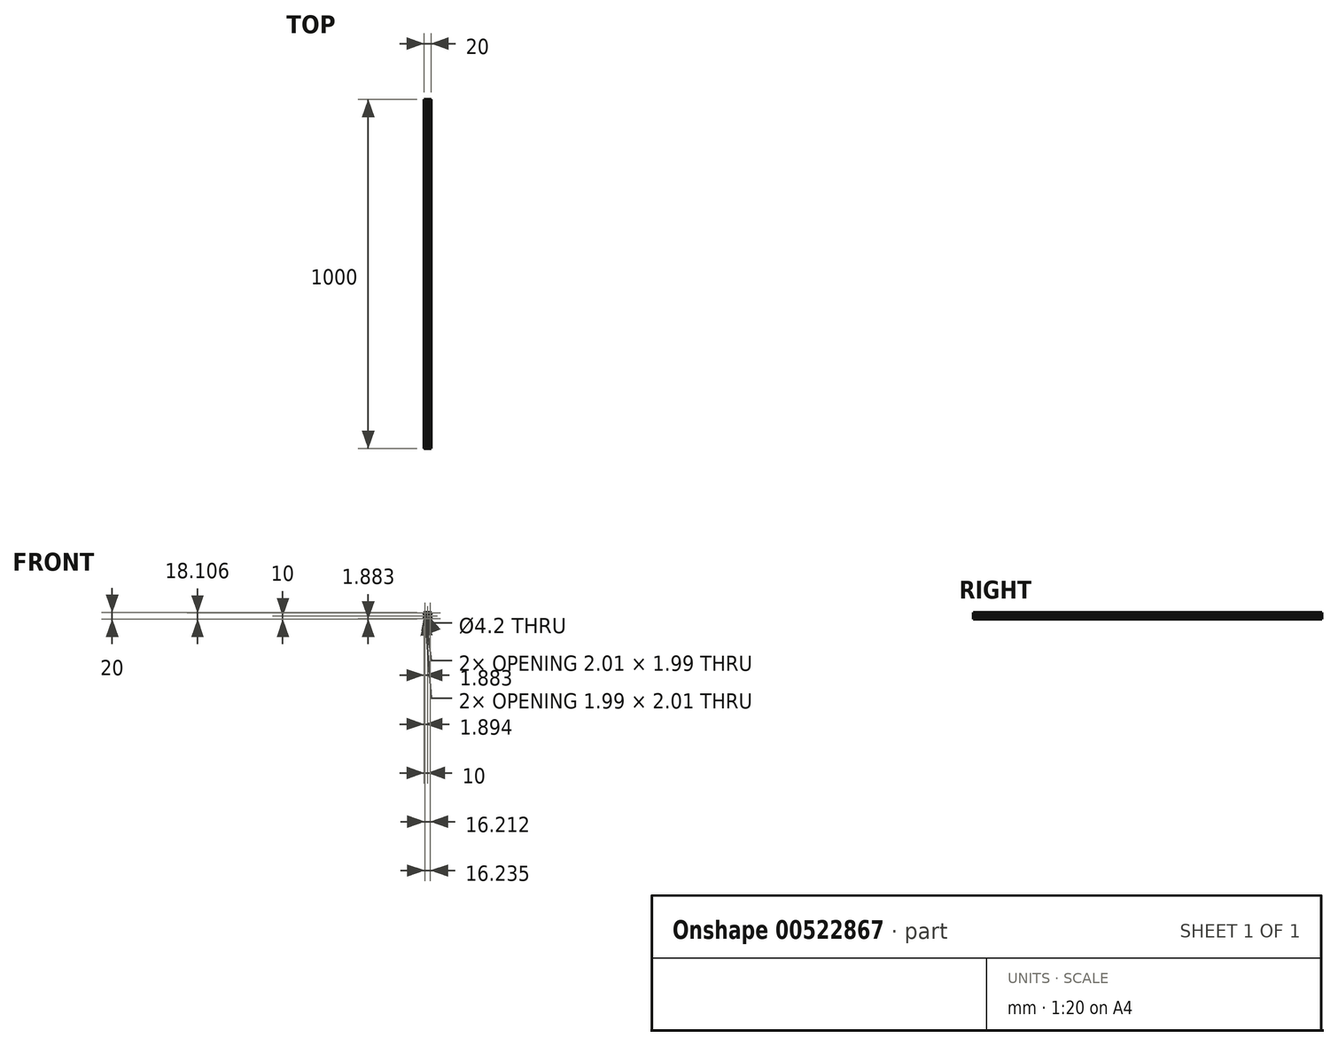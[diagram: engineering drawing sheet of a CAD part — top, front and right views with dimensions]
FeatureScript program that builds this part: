
annotation { "Feature Type Name" : "Feature", "Feature Type Description" : "" }
export const myFeature = defineFeature(function(context is Context, id is Id, definition is map)
    precondition{}
    {
        {
            var Q0;
            Q0=qCreatedBy(makeId("Front.planeOp"),FACE);
            var sketch = newSketch(context, id + "F0", { "sketchPlane" : qUnion([Q0])});
            skCircle(sketch, "E0", {"center": v(0, 0) * mm, "radius": 2.1 * mm});
            skLineSegment(sketch, "E1.bottom", {"start": v(-10, 10) * mm, "end": v(10, 10) * mm});
            skLineSegment(sketch, "E1.top", {"start": v(-10, -10) * mm, "end": v(10, -10) * mm});
            skLineSegment(sketch, "E1.left", {"start": v(-10, 10) * mm, "end": v(-10, -10) * mm});
            skLineSegment(sketch, "E1.right", {"start": v(10, 10) * mm, "end": v(10, -10) * mm});
            skLineSegment(sketch, "E2.bottom", {"start": v(-9.1, 9.1) * mm, "end": v(6.4, 9.1) * mm});
            skLineSegment(sketch, "E2.top", {"start": v(-9.1, -9.1) * mm, "end": v(9.1, -9.1) * mm});
            skLineSegment(sketch, "E2.left", {"start": v(-9.1, 9.1) * mm, "end": v(-9.1, -9.1) * mm});
            skLineSegment(sketch, "E2.right", {"start": v(9.1, 6.4) * mm, "end": v(9.1, -9.1) * mm});
            skLineSegment(sketch, "E3", {"start": v(-7.93, 7.93) * mm, "end": v(-1.48, 1.48) * mm});
            skLineSegment(sketch, "E4.0", {"start": v(7.46, 6.4) * mm, "end": v(1.92, 0.86) * mm});
            skLineSegment(sketch, "E5.MirrorCS", {"start": v(6.4, 7.46) * mm, "end": v(0.86, 1.92) * mm});
            skLineSegment(sketch, "E6.0", {"start": v(-8.47, 7.41) * mm, "end": v(-1.92, 0.86) * mm});
            skLineSegment(sketch, "E7.MirrorCS", {"start": v(-7.4, 8.46) * mm, "end": v(-0.86, 1.92) * mm});
            skPoint(sketch, "E8.orphan", {"position": v(-9.63, 8.57) * mm});
            skPoint(sketch, "E9.orphan", {"position": v(-8.57, 9.63) * mm});
            skPoint(sketch, "E10.orphan", {"position": v(8.05, 9.11) * mm});
            skPoint(sketch, "E11.orphan", {"position": v(9.11, 8.05) * mm});
            skPoint(sketch, "E12.orphan", {"position": v(9.63, -8.57) * mm});
            skPoint(sketch, "E13.orphan", {"position": v(8.57, -9.63) * mm});
            skPoint(sketch, "E14.orphan", {"position": v(-9.09, -10.15) * mm});
            skPoint(sketch, "E15.orphan", {"position": v(-10.15, -9.09) * mm});
            skLineSegment(sketch, "E16.trimOffspring", {"start": v(1.92, -0.86) * mm, "end": v(8.47, -7.41) * mm});
            skLineSegment(sketch, "E17.trimOffspring", {"start": v(0.86, -1.92) * mm, "end": v(7.4, -8.46) * mm});
            skLineSegment(sketch, "E18.trimOffspring", {"start": v(1.48, -1.48) * mm, "end": v(7.93, -7.93) * mm});
            skLineSegment(sketch, "E19.trimOffspring", {"start": v(-0.86, -1.92) * mm, "end": v(-7.41, -8.47) * mm});
            skLineSegment(sketch, "E20.trimOffspring", {"start": v(-1.48, -1.48) * mm, "end": v(-7.93, -7.93) * mm});
            skLineSegment(sketch, "E21.trimOffspring", {"start": v(-1.92, -0.86) * mm, "end": v(-8.46, -7.4) * mm});
            skLineSegment(sketch, "E22", {"start": v(-3.9, -2.84) * mm, "end": v(-3.9, 2.84) * mm});
            skLineSegment(sketch, "E23.1.0", {"start": v(2.84, -3.9) * mm, "end": v(-2.84, -3.9) * mm});
            skLineSegment(sketch, "E23.2.0", {"start": v(3.9, 2.84) * mm, "end": v(3.9, -2.84) * mm});
            skLineSegment(sketch, "E23.3.0", {"start": v(-2.84, 3.9) * mm, "end": v(2.84, 3.9) * mm});
            skLineSegment(sketch, "E24", {"start": v(-9.1, 2.84) * mm, "end": v(-9.1, -2.84) * mm});
            skLineSegment(sketch, "E25.1.0", {"start": v(-2.84, -9.1) * mm, "end": v(2.84, -9.1) * mm});
            skLineSegment(sketch, "E25.2.0", {"start": v(9.1, -2.84) * mm, "end": v(9.1, 2.84) * mm});
            skLineSegment(sketch, "E25.3.0", {"start": v(2.84, 9.1) * mm, "end": v(-2.84, 9.1) * mm});
            skLineSegment(sketch, "E26", {"start": v(-9.1, -2.84) * mm, "end": v(-10, -3.74) * mm});
            skLineSegment(sketch, "E27", {"start": v(-9.1, 2.84) * mm, "end": v(-10, 3.74) * mm});
            skLineSegment(sketch, "E28.1.0", {"start": v(-2.84, -9.1) * mm, "end": v(-3.74, -10) * mm});
            skLineSegment(sketch, "E28.1.1", {"start": v(2.84, -9.1) * mm, "end": v(3.74, -10) * mm});
            skLineSegment(sketch, "E28.2.0", {"start": v(9.1, -2.84) * mm, "end": v(10, -3.74) * mm});
            skLineSegment(sketch, "E28.2.1", {"start": v(9.1, 2.84) * mm, "end": v(10, 3.74) * mm});
            skLineSegment(sketch, "E28.3.0", {"start": v(2.84, 9.1) * mm, "end": v(3.74, 10) * mm});
            skLineSegment(sketch, "E28.3.1", {"start": v(-2.84, 9.1) * mm, "end": v(-3.74, 10) * mm});
            skLineSegment(sketch, "E29", {"start": v(-6.4, -9.1) * mm, "end": v(-6.4, -7.46) * mm});
            skLineSegment(sketch, "E30", {"start": v(-9.1, -6.4) * mm, "end": v(-7.46, -6.4) * mm});
            skLineSegment(sketch, "E31.1.0", {"start": v(6.4, -9.1) * mm, "end": v(6.4, -7.46) * mm});
            skLineSegment(sketch, "E31.1.1", {"start": v(9.1, -6.4) * mm, "end": v(7.46, -6.4) * mm});
            skLineSegment(sketch, "E31.2.0", {"start": v(9.1, 6.4) * mm, "end": v(7.46, 6.4) * mm});
            skLineSegment(sketch, "E31.2.1", {"start": v(6.4, 9.1) * mm, "end": v(6.4, 7.46) * mm});
            skLineSegment(sketch, "E31.3.0", {"start": v(-6.4, 9.1) * mm, "end": v(-6.4, 7.46) * mm});
            skLineSegment(sketch, "E31.3.1", {"start": v(-9.1, 6.4) * mm, "end": v(-7.46, 6.4) * mm});
            skPoint(sketch, "E32.start.orphan", {"position": v(9.1, 9.1) * mm});
            skLineSegment(sketch, "E33", {"start": v(7.47, 9.12) * mm, "end": v(9.1, 9.1) * mm});
            skLineSegment(sketch, "E34", {"start": v(9.1, 9.1) * mm, "end": v(9.1, 7.46) * mm});
            skLineSegment(sketch, "E35", {"start": v(7.47, 9.12) * mm, "end": v(7.11, 8.77) * mm});
            skLineSegment(sketch, "E36", {"start": v(9.1, 7.46) * mm, "end": v(8.74, 7.11) * mm});
            skLineSegment(sketch, "E37", {"start": v(8.74, 7.11) * mm, "end": v(7.11, 8.77) * mm});
            skLineSegment(sketch, "E38.1.0", {"start": v(-9.12, 7.47) * mm, "end": v(-8.77, 7.11) * mm});
            skLineSegment(sketch, "E38.1.1", {"start": v(-9.12, 7.47) * mm, "end": v(-9.1, 9.1) * mm});
            skLineSegment(sketch, "E38.1.2", {"start": v(-9.1, 9.1) * mm, "end": v(-7.46, 9.1) * mm});
            skLineSegment(sketch, "E38.1.3", {"start": v(-7.46, 9.1) * mm, "end": v(-7.11, 8.74) * mm});
            skLineSegment(sketch, "E38.1.4", {"start": v(-7.11, 8.74) * mm, "end": v(-8.77, 7.11) * mm});
            skLineSegment(sketch, "E38.2.0", {"start": v(-7.47, -9.12) * mm, "end": v(-7.11, -8.77) * mm});
            skLineSegment(sketch, "E38.2.1", {"start": v(-7.47, -9.12) * mm, "end": v(-9.1, -9.1) * mm});
            skLineSegment(sketch, "E38.2.2", {"start": v(-9.1, -9.1) * mm, "end": v(-9.1, -7.46) * mm});
            skLineSegment(sketch, "E38.2.3", {"start": v(-9.1, -7.46) * mm, "end": v(-8.74, -7.11) * mm});
            skLineSegment(sketch, "E38.2.4", {"start": v(-8.74, -7.11) * mm, "end": v(-7.11, -8.77) * mm});
            skLineSegment(sketch, "E38.3.0", {"start": v(9.12, -7.47) * mm, "end": v(8.77, -7.11) * mm});
            skLineSegment(sketch, "E38.3.1", {"start": v(9.12, -7.47) * mm, "end": v(9.1, -9.1) * mm});
            skLineSegment(sketch, "E38.3.2", {"start": v(9.1, -9.1) * mm, "end": v(7.46, -9.1) * mm});
            skLineSegment(sketch, "E38.3.3", {"start": v(7.46, -9.1) * mm, "end": v(7.11, -8.74) * mm});
            skLineSegment(sketch, "E38.3.4", {"start": v(7.11, -8.74) * mm, "end": v(8.77, -7.11) * mm});
            skSolve(sketch);
        }
        {
            var Q0;
            {var subQ5=sQuery(id+"F0.wireOp",EDGE,"E27");Q0=makeQuery(id+"F0.imprint","IMPRINT",FACE,{"disambiguationData":[TD([[makeQuery(id+"F0.imprint","IMPRINT",EDGE,{"derivedFrom":subQ5}),-1.0]])]});}
            var Q1;
            {var subQ0=sQuery(id+"F0.wireOp",EDGE,"E31.3.0");Q1=makeQuery(id+"F0.imprint","IMPRINT",FACE,{"disambiguationData":[TD([[makeQuery(id+"F0.imprint","IMPRINT",EDGE,{"derivedFrom":subQ0}),-1.0]])]});}
            var Q2;
            {var subQ0=sQuery(id+"F0.wireOp",EDGE,"E31.3.1");Q2=makeQuery(id+"F0.imprint","IMPRINT",FACE,{"disambiguationData":[TD([[makeQuery(id+"F0.imprint","IMPRINT",EDGE,{"derivedFrom":subQ0}),1.0]])]});}
            var Q3;
            {var subQ4=sQuery(id+"F0.wireOp",EDGE,"E3");Q3=makeQuery(id+"F0.imprint","IMPRINT",FACE,{"disambiguationData":[TD([[makeQuery(id+"F0.imprint","IMPRINT",EDGE,{"derivedFrom":subQ4}),-1.0]])]});}
            var Q4;
            {var subQ5=sQuery(id+"F0.wireOp",EDGE,"E3");Q4=makeQuery(id+"F0.imprint","IMPRINT",FACE,{"disambiguationData":[TD([[makeQuery(id+"F0.imprint","IMPRINT",EDGE,{"derivedFrom":subQ5}),1.0]])]});}
            var Q5;
            {var subQ0=sQuery(id+"F0.wireOp",EDGE,"E28.2.1");Q5=makeQuery(id+"F0.imprint","IMPRINT",FACE,{"disambiguationData":[TD([[makeQuery(id+"F0.imprint","IMPRINT",EDGE,{"derivedFrom":subQ0}),1.0]])]});}
            var Q6;
            {var subQ5=sQuery(id+"F0.wireOp",EDGE,"E23.2.0");Q6=makeQuery(id+"F0.imprint","IMPRINT",FACE,{"disambiguationData":[TD([[makeQuery(id+"F0.imprint","IMPRINT",EDGE,{"derivedFrom":subQ5}),-1.0]])]});}
            var Q7;
            {var subQ5=sQuery(id+"F0.wireOp",EDGE,"E23.3.0");Q7=makeQuery(id+"F0.imprint","IMPRINT",FACE,{"disambiguationData":[TD([[makeQuery(id+"F0.imprint","IMPRINT",EDGE,{"derivedFrom":subQ5}),-1.0]])]});}
            var Q8;
            {var subQ5=sQuery(id+"F0.wireOp",EDGE,"E22");Q8=makeQuery(id+"F0.imprint","IMPRINT",FACE,{"disambiguationData":[TD([[makeQuery(id+"F0.imprint","IMPRINT",EDGE,{"derivedFrom":subQ5}),-1.0]])]});}
            var Q9;
            {var subQ5=sQuery(id+"F0.wireOp",EDGE,"E23.1.0");Q9=makeQuery(id+"F0.imprint","IMPRINT",FACE,{"disambiguationData":[TD([[makeQuery(id+"F0.imprint","IMPRINT",EDGE,{"derivedFrom":subQ5}),-1.0]])]});}
            var Q10;
            {var subQ7=sQuery(id+"F0.wireOp",EDGE,"E20.trimOffspring");Q10=makeQuery(id+"F0.imprint","IMPRINT",FACE,{"disambiguationData":[TD([[makeQuery(id+"F0.imprint","IMPRINT",EDGE,{"derivedFrom":subQ7}),1.0]])]});}
            var Q11;
            {var subQ5=sQuery(id+"F0.wireOp",EDGE,"E20.trimOffspring");Q11=makeQuery(id+"F0.imprint","IMPRINT",FACE,{"disambiguationData":[TD([[makeQuery(id+"F0.imprint","IMPRINT",EDGE,{"derivedFrom":subQ5}),-1.0]])]});}
            var Q12;
            {var subQ7=sQuery(id+"F0.wireOp",EDGE,"E18.trimOffspring");Q12=makeQuery(id+"F0.imprint","IMPRINT",FACE,{"disambiguationData":[TD([[makeQuery(id+"F0.imprint","IMPRINT",EDGE,{"derivedFrom":subQ7}),-1.0]])]});}
            var Q13;
            {var subQ6=sQuery(id+"F0.wireOp",EDGE,"E18.trimOffspring");Q13=makeQuery(id+"F0.imprint","IMPRINT",FACE,{"disambiguationData":[TD([[makeQuery(id+"F0.imprint","IMPRINT",EDGE,{"derivedFrom":subQ6}),1.0]])]});}
            var Q14;
            {var subQ4=sQuery(id+"F0.wireOp",EDGE,"E28.1.1");Q14=makeQuery(id+"F0.imprint","IMPRINT",FACE,{"disambiguationData":[TD([[makeQuery(id+"F0.imprint","IMPRINT",EDGE,{"derivedFrom":subQ4}),1.0]])]});}
            var Q15;
            {var subQ0=sQuery(id+"F0.wireOp",EDGE,"E31.1.1");Q15=makeQuery(id+"F0.imprint","IMPRINT",FACE,{"disambiguationData":[TD([[makeQuery(id+"F0.imprint","IMPRINT",EDGE,{"derivedFrom":subQ0}),1.0]])]});}
            var Q16;
            {var subQ0=sQuery(id+"F0.wireOp",EDGE,"E31.1.0");Q16=makeQuery(id+"F0.imprint","IMPRINT",FACE,{"disambiguationData":[TD([[makeQuery(id+"F0.imprint","IMPRINT",EDGE,{"derivedFrom":subQ0}),-1.0]])]});}
            var Q17;
            {var subQ4=sQuery(id+"F0.wireOp",EDGE,"E26");Q17=makeQuery(id+"F0.imprint","IMPRINT",FACE,{"disambiguationData":[TD([[makeQuery(id+"F0.imprint","IMPRINT",EDGE,{"derivedFrom":subQ4}),1.0]])]});}
            var Q18;
            {var subQ7=sQuery(id+"F0.wireOp",EDGE,"E29");Q18=makeQuery(id+"F0.imprint","IMPRINT",FACE,{"disambiguationData":[TD([[makeQuery(id+"F0.imprint","IMPRINT",EDGE,{"derivedFrom":subQ7}),1.0]])]});}
            var Q19;
            {var subQ1=sQuery(id+"F0.wireOp",EDGE,"E30");Q19=makeQuery(id+"F0.imprint","IMPRINT",FACE,{"disambiguationData":[TD([[makeQuery(id+"F0.imprint","IMPRINT",EDGE,{"derivedFrom":subQ1}),-1.0]])]});}
            extrude(context, id + "F1", {"entities" : qUnion([Q0, Q1, Q2, Q3, Q4, Q5, Q6, Q7, Q8, Q9, Q10, Q11, Q12, Q13, Q14, Q15, Q16, Q17, Q18, Q19]), "depth" : 1000 * mm, "offsetDistance" : 25 * mm});
        }
        {
            var Q0;
            Q0=makeQuery(id+"F1.opExtrude","SWEPT_EDGE",EDGE,{"disambiguationData":[OSD([sQuery(id+"F0.wireOp",EDGE,"E1.bottom"),sQuery(id+"F0.wireOp",EDGE,"E1.right")])]});
            var Q1;
            Q1=makeQuery(id+"F1.opExtrude","SWEPT_EDGE",EDGE,{"disambiguationData":[OSD([sQuery(id+"F0.wireOp",EDGE,"E1.bottom"),sQuery(id+"F0.wireOp",EDGE,"E1.left")])]});
            var Q2;
            Q2=makeQuery(id+"F1.opExtrude","SWEPT_EDGE",EDGE,{"disambiguationData":[OSD([sQuery(id+"F0.wireOp",EDGE,"E1.top"),sQuery(id+"F0.wireOp",EDGE,"E1.left")])]});
            var Q3;
            Q3=makeQuery(id+"F1.opExtrude","SWEPT_EDGE",EDGE,{"disambiguationData":[OSD([sQuery(id+"F0.wireOp",EDGE,"E1.top"),sQuery(id+"F0.wireOp",EDGE,"E1.right")])]});
            fillet(context, id + "F2", {"entities" : qUnion([Q0, Q1, Q2, Q3]), "radius" : 1.5 * mm, "tangentPropagation" : true, "allowEdgeOverflow" : false});
        }
        {
            var Q0;
            {var subQ0=sQuery(id+"F0.wireOp",EDGE,"E1.bottom");Q0=makeQuery(id+"F1.opExtrude","SWEPT_FACE",FACE,{"disambiguationData":[OSD([subQ0]),TDD([makeQuery(id+"F0.imprint","IMPRINT",EDGE,{"disambiguationData":[TD([[makeQuery(id+"F0.imprint","INTERSECT",VERTEX,{"derivedFrom":[subQ0,sQuery(id+"F0.wireOp",EDGE,"E1.left")]}),-1.0]])],"derivedFrom":subQ0})])]});}
            var sketch = newSketch(context, id + "F3", { "sketchPlane" : qUnion([Q0])});
            skLineSegment(sketch, "E39.bottom", {"start": v(10, -10) * mm, "end": v(-10, -10) * mm});
            skLineSegment(sketch, "E39.top", {"start": v(10, 10) * mm, "end": v(-10, 10) * mm});
            skLineSegment(sketch, "E39.left", {"start": v(10, -10) * mm, "end": v(10, 10) * mm});
            skLineSegment(sketch, "E39.right", {"start": v(-10, -10) * mm, "end": v(-10, 10) * mm});
            skPoint(sketch, "E39.middle", {"position": v(0, 0) * mm});
            skSolve(sketch);
        }
    });
